# Revit family: JOMA_420 & 425
name_source: partatom
category: Structural Connections
revit_build: Autodesk Revit Structure 2012 (Build: 20110309_2315(x64)
units: mm (PartAtom-declared; Revit-internal decimal feet)

## types (2) — shared parameters
Länk Joma Dimensioneringsverktyg = http://www.joma.se
Material = Varmförzinkad stålplåt
b = 55 mm  [stored 0.180446 ft]
ir = 3.843 mm  [stored 0.0126083 ft]
t = 3 mm  [stored 0.00984252 ft]
yr = 6.843 mm  [stored 0.0224508 ft]
zero-valued in all types: Default Elevation

## per-type parameters (varying)
| type | Typ | Vikt | Vinkelbeslag 420 | Vinkelbeslag 425 | h | l |
| 4200000 | VINKEL 420 | 0,14 | Yes | No | 65 mm  [stored 0.213255 ft] | 65 mm  [stored 0.213255 ft] |
| 4250000 | VINKEL 425 | 0,142 | No | Yes | 80 mm  [stored 0.262467 ft] | 50 mm  [stored 0.164042 ft] |

note: [stored X ft] marks values corroborated as IEEE doubles in the binary element streams (Revit-internal decimal feet)

## geometry (parser evidence)
native form markers: Sweep x2
no freeform markers — native parametric forms only
